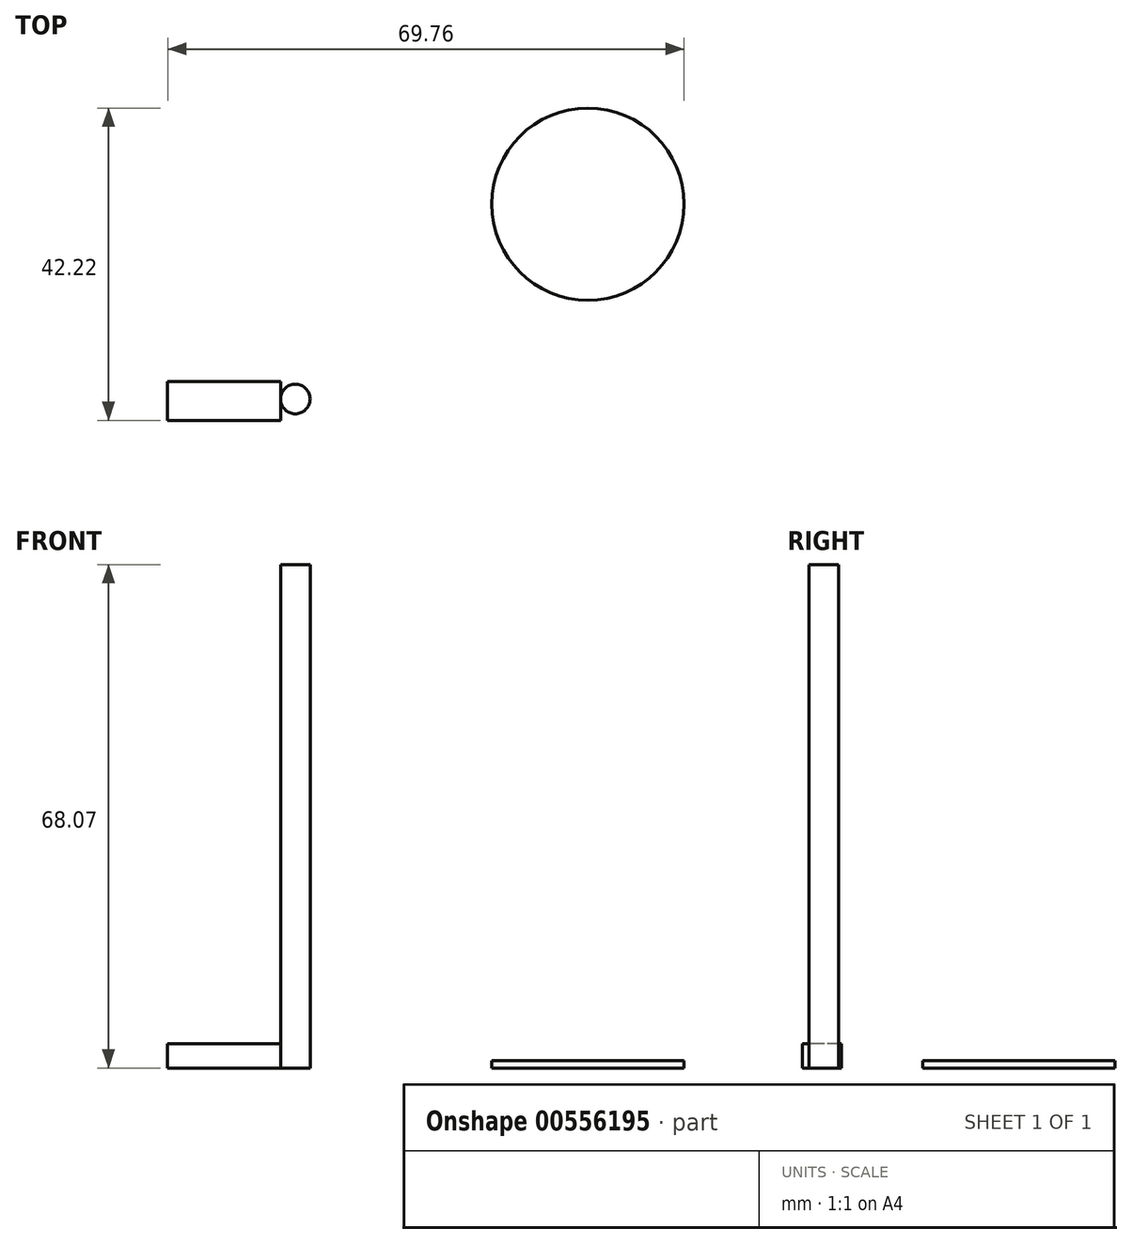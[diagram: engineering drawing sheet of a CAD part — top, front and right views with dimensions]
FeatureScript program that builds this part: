
annotation { "Feature Type Name" : "Feature", "Feature Type Description" : "" }
export const myFeature = defineFeature(function(context is Context, id is Id, definition is map)
    precondition{}
    {
        {
            var Q0;
            Q0=qCreatedBy(makeId("Top.planeOp"),FACE);
            var sketch = newSketch(context, id + "F0", { "sketchPlane" : qUnion([Q0])});
            skLineSegment(sketch, "E0.bottom", {"start": v(-19.73, 8.62) * mm, "end": v(-34.97, 8.62) * mm});
            skLineSegment(sketch, "E0.top", {"start": v(-19.73, 3.35) * mm, "end": v(-34.97, 3.35) * mm});
            skLineSegment(sketch, "E0.left", {"start": v(-19.73, 8.62) * mm, "end": v(-19.73, 3.35) * mm});
            skLineSegment(sketch, "E0.right", {"start": v(-34.97, 8.62) * mm, "end": v(-34.97, 3.35) * mm});
            skCircle(sketch, "E1", {"center": v(-17.73, 6.23) * mm, "radius": 2 * mm});
            skCircle(sketch, "E2", {"center": v(21.8, 32.58) * mm, "radius": 12.99 * mm});
            skCircle(sketch, "E3", {"center": v(21.8, 32.58) * mm, "radius": 13.04 * mm});
            skSolve(sketch);
        }
        {
            var Q0;
            Q0=makeQuery(id+"F0.imprint","IMPRINT",FACE,{"disambiguationData":[TD([[makeQuery(id+"F0.imprint","IMPRINT",EDGE,{"derivedFrom":sQuery(id+"F0.wireOp",EDGE,"E1")}),1.0]])]});
            extrude(context, id + "F1", {"entities" : qUnion([Q0]), "depth" : 68.07 * mm, "offsetDistance" : 25.4 * mm});
        }
        {
            var Q0;
            {var subQ3=sQuery(id+"F0.wireOp",EDGE,"E0.bottom");Q0=makeQuery(id+"F0.imprint","IMPRINT",FACE,{"disambiguationData":[TD([[makeQuery(id+"F0.imprint","IMPRINT",EDGE,{"derivedFrom":subQ3}),1.0]])]});}
            extrude(context, id + "F2", {"entities" : qUnion([Q0]), "operationType" : NewBodyOperationType.ADD, "depth" : 3.3 * mm, "offsetDistance" : 25.4 * mm});
        }
        {
            var Q0;
            Q0=makeQuery(id+"F0.imprint","IMPRINT",FACE,{"disambiguationData":[TD([[makeQuery(id+"F0.imprint","IMPRINT",EDGE,{"derivedFrom":sQuery(id+"F0.wireOp",EDGE,"E2")}),1.0]])]});
            extrude(context, id + "F3", {"entities" : qUnion([Q0]), "depth" : 1.02 * mm, "offsetDistance" : 25.4 * mm});
        }
    });
